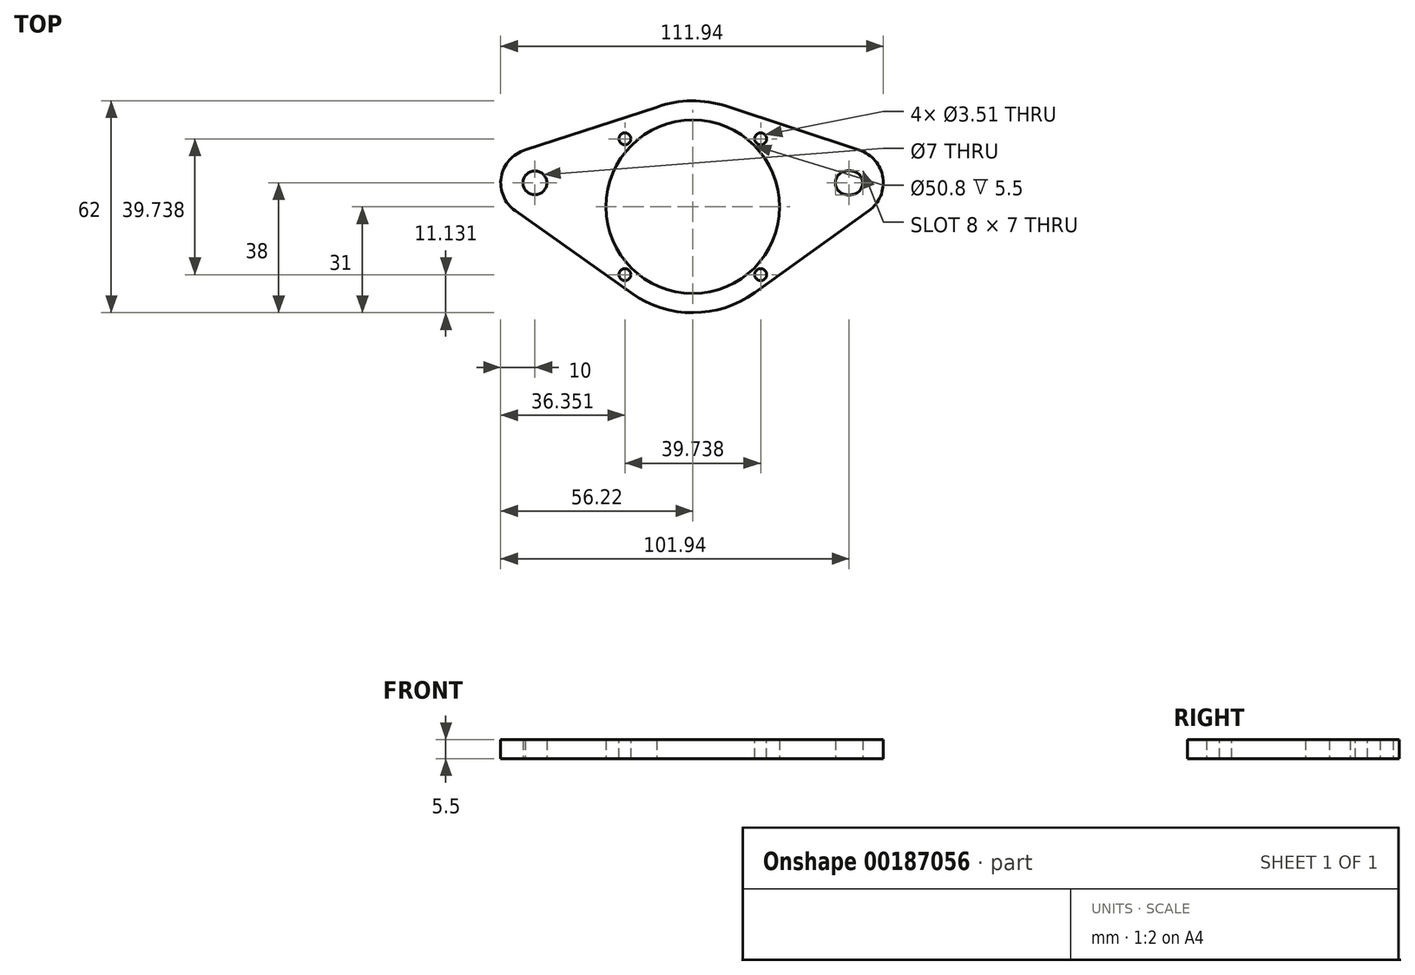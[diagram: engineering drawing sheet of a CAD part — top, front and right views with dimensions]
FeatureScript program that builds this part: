
annotation { "Feature Type Name" : "Feature", "Feature Type Description" : "" }
export const myFeature = defineFeature(function(context is Context, id is Id, definition is map)
    precondition{}
    {
        {
            var Q0;
            Q0=qCreatedBy(makeId("Top.planeOp"),FACE);
            var sketch = newSketch(context, id + "F0", { "sketchPlane" : qUnion([Q0])});
            skLineSegment(sketch, "E0", {"start": v(0, 0) * mm, "end": v(91.44, 0) * mm, "construction": true});
            skCircle(sketch, "E1", {"center": v(0, 0) * mm, "radius": 3.5 * mm});
            skArc(sketch, "E2", {"start": v(91.44, 3.5) * mm, "mid": v(87.94, 0) * mm, "end": v(91.44, -3.5) * mm});
            skArc(sketch, "E3", {"start": v(92.44, -3.5) * mm, "mid": v(95.94, 0) * mm, "end": v(92.44, 3.5) * mm});
            skLineSegment(sketch, "E4", {"start": v(91.44, 3.5) * mm, "end": v(92.44, 3.5) * mm});
            skLineSegment(sketch, "E5", {"start": v(91.44, -3.5) * mm, "end": v(92.44, -3.5) * mm});
            skLineSegment(sketch, "E6", {"start": v(29.43, 24) * mm, "end": v(57.7, 24) * mm, "construction": true});
            skLineSegment(sketch, "E7", {"start": v(28.24, -38) * mm, "end": v(58.5, -38) * mm, "construction": true});
            skLineSegment(sketch, "E8", {"start": v(46.22, 24) * mm, "end": v(46.22, -38) * mm, "construction": true});
            skArc(sketch, "E9", {"start": v(-2.8, 9.6) * mm, "mid": v(-9.86, 1.65) * mm, "end": v(-5.78, -8.16) * mm});
            skArc(sketch, "E10", {"start": v(97.78, -8.12) * mm, "mid": v(101.82, 1.51) * mm, "end": v(95.08, 9.5) * mm});
            skLineSegment(sketch, "E11", {"start": v(-10, 0) * mm, "end": v(-10, 26.7) * mm, "construction": true});
            skLineSegment(sketch, "E12", {"start": v(101.94, 0) * mm, "end": v(101.94, 30.48) * mm, "construction": true});
            skCircle(sketch, "E13", {"center": v(46.22, -7) * mm, "radius": 31 * mm});
            skLineSegment(sketch, "E14", {"start": v(55.95, 22.43) * mm, "end": v(95.08, 9.5) * mm});
            skLineSegment(sketch, "E15", {"start": v(97.78, -8.12) * mm, "end": v(64.31, -32.17) * mm});
            skLineSegment(sketch, "E16", {"start": v(28.3, -32.3) * mm, "end": v(-5.78, -8.16) * mm});
            skPoint(sketch, "E17.orphan", {"position": v(-17.3, 0) * mm});
            skLineSegment(sketch, "E18.trimOffspring", {"start": v(-3.4, 9.4) * mm, "end": v(35.7, 22.16) * mm});
            skCircle(sketch, "E19", {"center": v(46.22, -7) * mm, "radius": 25.4 * mm});
            skSolve(sketch);
        }
        {
            var Q0;
            Q0 = qSketchRegion(id + "F0", true);
            extrude(context, id + "F1", {"entities" : qUnion([Q0]), "depth" : 5.5 * mm});
        }
        {
            var Q0;
            Q0=makeQuery(id+"F0.imprint","IMPRINT",FACE,{"disambiguationData":[TD([[makeQuery(id+"F0.imprint","IMPRINT",EDGE,{"derivedFrom":sQuery(id+"F0.wireOp",EDGE,"E19")}),-1.0]])]});
            var Q1;
            Q1=makeQuery(id+"F0.imprint","IMPRINT",FACE,{"disambiguationData":[TD([[makeQuery(id+"F0.imprint","IMPRINT",EDGE,{"derivedFrom":sQuery(id+"F0.wireOp",EDGE,"E19")}),1.0]])]});
            extrude(context, id + "F2", {"entities" : qUnion([Q0, Q1]), "operationType" : NewBodyOperationType.ADD, "oppositeDirection" : true, "depth" : 33 * mm});
        }
        {
            var Q0;
            Q0=makeQuery(id+"F0.imprint","IMPRINT",FACE,{"disambiguationData":[TD([[makeQuery(id+"F0.imprint","IMPRINT",EDGE,{"derivedFrom":sQuery(id+"F0.wireOp",EDGE,"E19")}),1.0]])]});
            extrude(context, id + "F3", {"entities" : qUnion([Q0]), "operationType" : NewBodyOperationType.REMOVE, "oppositeDirection" : true, "depth" : 28 * mm});
        }
        {
            var Q0;
            Q0=makeQuery(id+"F2.opExtrude","CAP_FACE",FACE,{"disambiguationData":[OSD([sQuery(id+"F0.wireOp",EDGE,"E13")])],"isStart":false});
            var sketch = newSketch(context, id + "F4", { "sketchPlane" : qUnion([Q0])});
            skCircle(sketch, "E20", {"center": v(46.22, 7) * mm, "radius": 2.5 * mm});
            skSolve(sketch);
        }
        {
            var Q0;
            Q0 = qSketchRegion(id + "F4", true);
            extrude(context, id + "F5", {"entities" : qUnion([Q0]), "operationType" : NewBodyOperationType.REMOVE, "oppositeDirection" : true, "depth" : 25.4 * mm});
        }
        {
            var Q0;
            {var subQ0=sQuery(id+"F0.wireOp",EDGE,"E16");var subQ2=sQuery(id+"F0.wireOp",EDGE,"E13");Q0=makeQuery(id+"F2.boolean.opBoolean","SPLIT",EDGE,{"disambiguationData":[TD([makeQuery(id+"F1.opExtrude","SWEPT_FACE",FACE,{"disambiguationData":[OSD([subQ0])]})])],"derivedFrom":makeQuery(id+"F2.opExtrude","CAP_EDGE",EDGE,{"disambiguationData":[OSD([subQ2])],"isStart":true})});}
            var Q1;
            {var subQ0=sQuery(id+"F0.wireOp",EDGE,"E14");var subQ1=sQuery(id+"F0.wireOp",EDGE,"E13");Q1=makeQuery(id+"F2.boolean.opBoolean","SPLIT",EDGE,{"disambiguationData":[TD([makeQuery(id+"F1.opExtrude","SWEPT_FACE",FACE,{"disambiguationData":[OSD([subQ0])]})])],"derivedFrom":makeQuery(id+"F2.opExtrude","CAP_EDGE",EDGE,{"disambiguationData":[OSD([subQ1])],"isStart":true})});}
            var Q2;
            Q2=makeQuery(id+"F2.opExtrude","CAP_EDGE",EDGE,{"disambiguationData":[OSD([sQuery(id+"F0.wireOp",EDGE,"E13")])],"isStart":false});
            fillet(context, id + "F6", {"entities" : qUnion([Q0, Q1, Q2]), "radius" : 5.08 * mm, "tangentPropagation" : true, "allowEdgeOverflow" : false});
        }
        {
            var Q0;
            Q0=makeQuery(id+"F2.opExtrude","CAP_FACE",FACE,{"disambiguationData":[OSD([sQuery(id+"F0.wireOp",EDGE,"E13")])],"isStart":false});
            var sketch = newSketch(context, id + "F7", { "sketchPlane" : qUnion([Q0])});
            skCircle(sketch, "E21", {"center": v(46.22, 7) * mm, "radius": 40.64 * mm});
            skSolve(sketch);
        }
        {
            var Q0;
            Q0 = qSketchRegion(id + "F7", true);
            var Q1;
            {var subQ0=sQuery(id+"F0.wireOp",EDGE,"E15");var subQ1=sQuery(id+"F0.wireOp",EDGE,"E13");var subQ2=sQuery(id+"F0.wireOp",EDGE,"E16");var subQ3=sQuery(id+"F0.wireOp",EDGE,"E14");var subQ4=sQuery(id+"F0.wireOp",EDGE,"E18.trimOffspring");var subQ5=sQuery(id+"F0.wireOp",EDGE,"E9");var subQ6=sQuery(id+"F0.wireOp",EDGE,"E1");Q1=makeQuery(id+"F2.boolean.opBoolean","SPLIT",FACE,{"disambiguationData":[TD([makeQuery(id+"F1.opExtrude","SWEPT_FACE",FACE,{"disambiguationData":[OSD([subQ6])]})])],"derivedFrom":makeQuery(id+"F1.opExtrude","CAP_FACE",FACE,{"disambiguationData":[OSD([subQ6,sQuery(id+"F0.wireOp",EDGE,"E2"),sQuery(id+"F0.wireOp",EDGE,"E3"),sQuery(id+"F0.wireOp",EDGE,"E4"),sQuery(id+"F0.wireOp",EDGE,"E5"),subQ5,sQuery(id+"F0.wireOp",EDGE,"E10"),subQ1,subQ3,subQ0,subQ2,subQ4,sQuery(id+"F0.wireOp",EDGE,"E19")])],"isStart":true})});}
            extrude(context, id + "F8", {"entities" : qUnion([Q0]), "operationType" : NewBodyOperationType.REMOVE, "endBound" : BoundingType.UP_TO_SURFACE, "oppositeDirection" : true, "endBoundEntityFace" : qUnion([Q1]), "depth" : 25.4 * mm});
        }
        {
            var Q0;
            Q0=makeQuery(id+"F1.opExtrude","CAP_FACE",FACE,{"disambiguationData":[OSD([sQuery(id+"F0.wireOp",EDGE,"E1"),sQuery(id+"F0.wireOp",EDGE,"E2"),sQuery(id+"F0.wireOp",EDGE,"E3"),sQuery(id+"F0.wireOp",EDGE,"E4"),sQuery(id+"F0.wireOp",EDGE,"E5"),sQuery(id+"F0.wireOp",EDGE,"E9"),sQuery(id+"F0.wireOp",EDGE,"E10"),sQuery(id+"F0.wireOp",EDGE,"E13"),sQuery(id+"F0.wireOp",EDGE,"E14"),sQuery(id+"F0.wireOp",EDGE,"E15"),sQuery(id+"F0.wireOp",EDGE,"E16"),sQuery(id+"F0.wireOp",EDGE,"E18.trimOffspring"),sQuery(id+"F0.wireOp",EDGE,"E19")])],"isStart":false});
            var sketch = newSketch(context, id + "F9", { "sketchPlane" : qUnion([Q0])});
            skCircle(sketch, "E22", {"center": v(46.22, -7) * mm, "radius": 28.1 * mm, "construction": true});
            skLineSegment(sketch, "E23", {"start": v(46.22, -7) * mm, "end": v(46.22, 21.1) * mm, "construction": true});
            skCircle(sketch, "E24", {"center": v(26.35, 12.87) * mm, "radius": 1.75 * mm});
            skLineSegment(sketch, "E25", {"start": v(46.22, -7) * mm, "end": v(26.35, 12.87) * mm, "construction": true});
            skCircle(sketch, "E26.1.0", {"center": v(26.35, -26.87) * mm, "radius": 1.75 * mm});
            skCircle(sketch, "E26.2.0", {"center": v(66.09, -26.87) * mm, "radius": 1.75 * mm});
            skCircle(sketch, "E26.3.0", {"center": v(66.09, 12.87) * mm, "radius": 1.75 * mm});
            skSolve(sketch);
        }
        {
            var Q0;
            Q0 = qSketchRegion(id + "F9", true);
            extrude(context, id + "F10", {"entities" : qUnion([Q0]), "operationType" : NewBodyOperationType.REMOVE, "endBound" : BoundingType.THROUGH_ALL, "oppositeDirection" : true, "depth" : 25.4 * mm});
        }
    });
